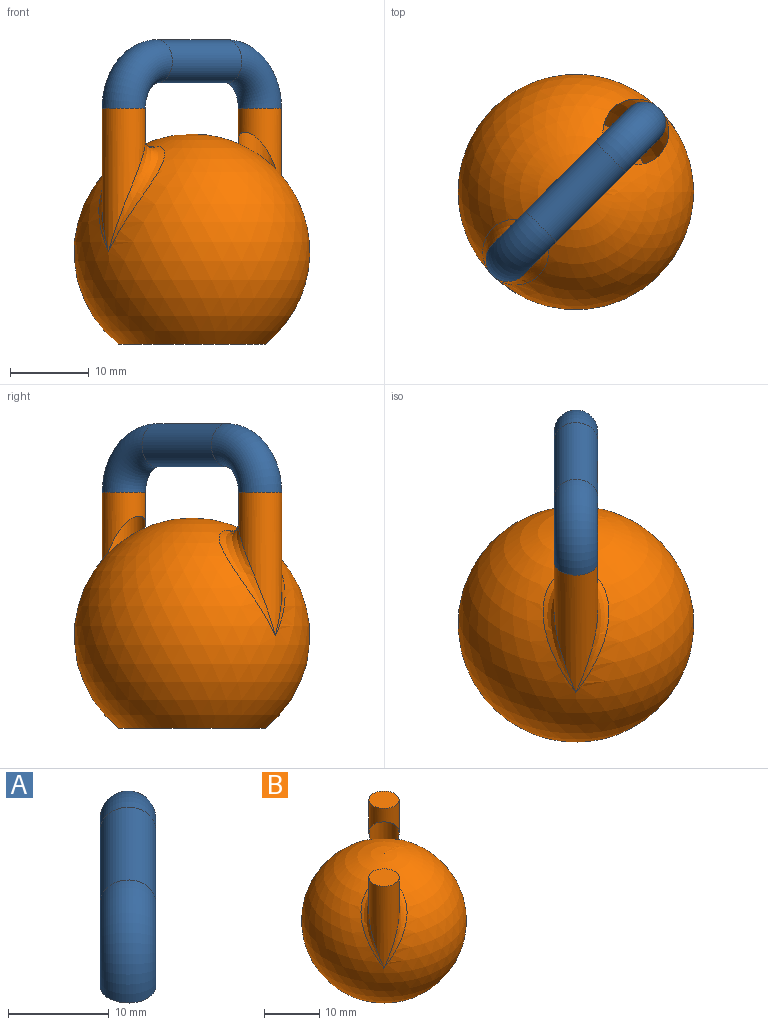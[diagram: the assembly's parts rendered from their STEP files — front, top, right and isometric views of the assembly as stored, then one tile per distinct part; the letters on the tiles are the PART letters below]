
ASSEMBLY  parts=2 mates=1
PART A: 5 faces, bbox 22.8x22.8x9.5 mm
  f0: plane 5.5x5.5mm, normal (0,0,-1), area 23.8mm2, adj f2
  f1: plane 5.5x5.5mm, normal (0,0,-1), area 23.8mm2, adj f4
  f2: torus R=6mm, axis (-0.71,0.71,0), area 162.8mm2, adj f0,f3
  f3: cylinder r=2.75mm len=12.73mm, axis (0.71,0.71,0), area 216mm2, adj f2,f4
  f4: torus R=6mm, axis (-0.71,0.71,0), area 162.8mm2, adj f1,f3
PART B: 8 faces, bbox 30x30x30 mm
  f0: sphere r=15mm, area 2326.2mm2, adj f1,f2,f3
  f1: plane 18.65x18.65mm, normal (0,0,-1), area 273.1mm2, adj f0
  f2: bspline ~15.24x8.38mm, area -2.3mm2, adj f0,f4
  f3: bspline ~15.26x8.39mm, area 71.6mm2, adj f0,f5
  f4: cylinder r=2.75mm len=18.25mm, axis (0,0,1), area 147.6mm2, adj f2,f6
  f5: cylinder r=2.75mm len=18.25mm, axis (0,0,1), area 147.6mm2, adj f3,f7
  f6: plane 5.5x5.5mm, normal (0,0,-1), area 23.8mm2, adj f4
  f7: plane 5.5x5.5mm, normal (0,0,1), area 23.8mm2, adj f5
PLACE A t=(-43.99,-16.6,-5.21)mm
PLACE B t=(-43.99,-16.6,-5.21)mm fixed
MATE fastened A.f0 <-> B.f5  axis (0,0,-1) through (-12,15.39,29.79)mm
